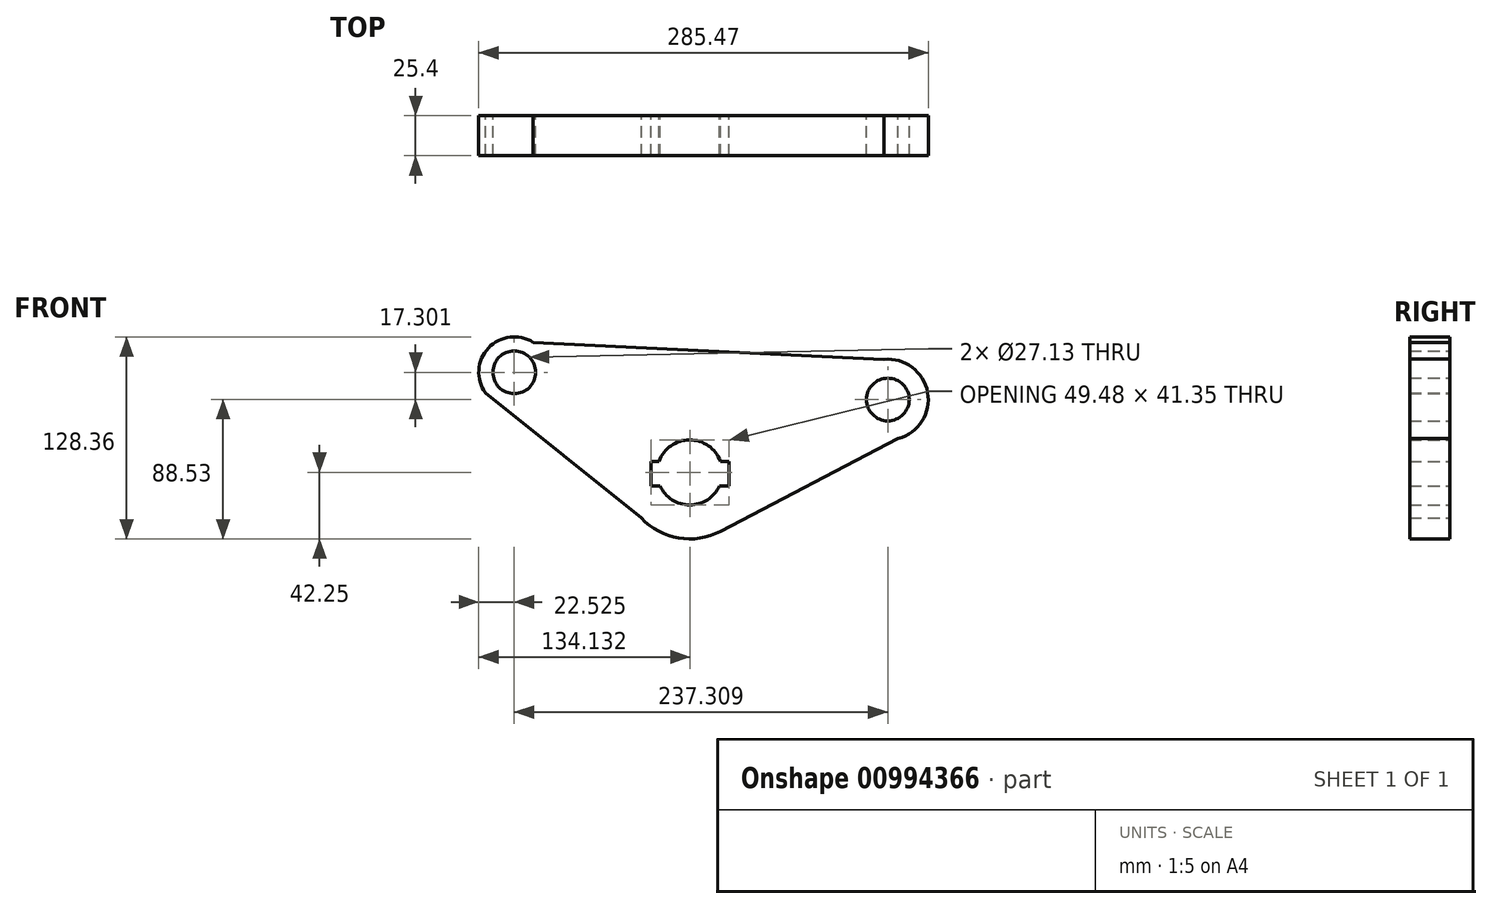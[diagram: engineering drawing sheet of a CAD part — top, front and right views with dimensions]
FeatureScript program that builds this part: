
annotation { "Feature Type Name" : "Feature", "Feature Type Description" : "" }
export const myFeature = defineFeature(function(context is Context, id is Id, definition is map)
    precondition{}
    {
        {
            var Q0;
            Q0=qCreatedBy(makeId("Front.planeOp"),FACE);
            var sketch = newSketch(context, id + "F0", { "sketchPlane" : qUnion([Q0])});
            skCircle(sketch, "E0", {"center": v(0, 0) * mm, "radius": 42.25 * mm});
            skCircle(sketch, "E1", {"center": v(125.87, 46.28) * mm, "radius": 25.63 * mm});
            skLineSegment(sketch, "E2", {"start": v(132.42, 21.5) * mm, "end": v(19.56, -37.45) * mm});
            skCircle(sketch, "E3", {"center": v(0, 0) * mm, "radius": 20.68 * mm});
            skCircle(sketch, "E4", {"center": v(125.87, 46.28) * mm, "radius": 13.56 * mm});
            skCircle(sketch, "E5", {"center": v(-111.44, 63.58) * mm, "radius": 22.52 * mm});
            skLineSegment(sketch, "E6", {"start": v(-99.42, 82.63) * mm, "end": v(123.37, 71.79) * mm});
            skCircle(sketch, "E7", {"center": v(-111.44, 63.58) * mm, "radius": 13.56 * mm});
            skLineSegment(sketch, "E8", {"start": v(-129.8, 50.54) * mm, "end": v(-21.66, -36.28) * mm});
            skLineSegment(sketch, "E9.bottom", {"start": v(-24.57, 7.05) * mm, "end": v(24.91, 7.05) * mm});
            skLineSegment(sketch, "E9.top", {"start": v(-24.57, -8.5) * mm, "end": v(24.91, -8.5) * mm});
            skLineSegment(sketch, "E9.left", {"start": v(-24.57, 7.05) * mm, "end": v(-24.57, -8.5) * mm});
            skLineSegment(sketch, "E9.right", {"start": v(24.91, 7.05) * mm, "end": v(24.91, -8.5) * mm});
            skSolve(sketch);
        }
        {
            var Q0;
            Q0=makeQuery(id+"F0.imprint","IMPRINT",FACE,{"disambiguationData":[TD([[makeQuery(id+"F0.imprint","IMPRINT",EDGE,{"derivedFrom":sQuery(id+"F0.wireOp",EDGE,"E7")}),1.0]])]});
            var Q1;
            Q1=makeQuery(id+"F0.imprint","IMPRINT",FACE,{"disambiguationData":[TD([[makeQuery(id+"F0.imprint","IMPRINT",EDGE,{"derivedFrom":sQuery(id+"F0.wireOp",EDGE,"E7")}),-1.0]])]});
            var Q2;
            {var subQ0=sQuery(id+"F0.wireOp",EDGE,"E9.top");var subQ1=sQuery(id+"F0.wireOp",EDGE,"E3");var subQ2=makeQuery(id+"F0.imprint","INTERSECT",VERTEX,{"disambiguationData":[OD(0.0)],"derivedFrom":[subQ1,subQ0]});Q2=makeQuery(id+"F0.imprint","IMPRINT",FACE,{"disambiguationData":[TD([[makeQuery(id+"F0.imprint","IMPRINT",EDGE,{"disambiguationData":[TD([[subQ2,-1.0]])],"derivedFrom":subQ1}),1.0]])]});}
            var Q3;
            Q3=makeQuery(id+"F0.imprint","IMPRINT",FACE,{"disambiguationData":[TD([[makeQuery(id+"F0.imprint","IMPRINT",EDGE,{"derivedFrom":sQuery(id+"F0.wireOp",EDGE,"E4")}),1.0]])]});
            var Q4;
            {var subQ0=sQuery(id+"F0.wireOp",EDGE,"E9.left");Q4=makeQuery(id+"F0.imprint","IMPRINT",FACE,{"disambiguationData":[TD([[makeQuery(id+"F0.imprint","IMPRINT",EDGE,{"derivedFrom":subQ0}),-1.0]])]});}
            var Q5;
            {var subQ0=sQuery(id+"F0.wireOp",EDGE,"E9.bottom");var subQ1=sQuery(id+"F0.wireOp",EDGE,"E3");var subQ2=makeQuery(id+"F0.imprint","INTERSECT",VERTEX,{"disambiguationData":[OD(0.0)],"derivedFrom":[subQ1,subQ0]});Q5=makeQuery(id+"F0.imprint","IMPRINT",FACE,{"disambiguationData":[TD([[makeQuery(id+"F0.imprint","IMPRINT",EDGE,{"disambiguationData":[TD([[subQ2,-1.0]])],"derivedFrom":subQ1}),1.0]])]});}
            var Q6;
            {var subQ0=sQuery(id+"F0.wireOp",EDGE,"E9.bottom");var subQ1=sQuery(id+"F0.wireOp",EDGE,"E3");var subQ2=makeQuery(id+"F0.imprint","INTERSECT",VERTEX,{"disambiguationData":[OD(0.0)],"derivedFrom":[subQ1,subQ0]});Q6=makeQuery(id+"F0.imprint","IMPRINT",FACE,{"disambiguationData":[TD([[makeQuery(id+"F0.imprint","IMPRINT",EDGE,{"disambiguationData":[TD([[subQ2,1.0]])],"derivedFrom":subQ1}),1.0]])]});}
            var Q7;
            {var subQ0=sQuery(id+"F0.wireOp",EDGE,"E8");var subQ1=sQuery(id+"F0.wireOp",EDGE,"E5");var subQ2=makeQuery(id+"F0.imprint","INTERSECT",VERTEX,{"disambiguationData":[OD(0.0)],"derivedFrom":[subQ1,subQ0]});Q7=makeQuery(id+"F0.imprint","IMPRINT",FACE,{"disambiguationData":[TD([[makeQuery(id+"F0.imprint","IMPRINT",EDGE,{"disambiguationData":[TD([[subQ2,-1.0]])],"derivedFrom":subQ1}),1.0]])]});}
            var Q8;
            {var subQ0=sQuery(id+"F0.wireOp",EDGE,"E8");var subQ1=sQuery(id+"F0.wireOp",EDGE,"E0");var subQ2=makeQuery(id+"F0.imprint","INTERSECT",VERTEX,{"disambiguationData":[OD(0.0)],"derivedFrom":[subQ1,subQ0]});Q8=makeQuery(id+"F0.imprint","IMPRINT",FACE,{"disambiguationData":[TD([[makeQuery(id+"F0.imprint","IMPRINT",EDGE,{"disambiguationData":[TD([[subQ2,1.0]])],"derivedFrom":subQ1}),1.0]])]});}
            var Q9;
            {var subQ5=sQuery(id+"F0.wireOp",EDGE,"E9.right");Q9=makeQuery(id+"F0.imprint","IMPRINT",FACE,{"disambiguationData":[TD([[makeQuery(id+"F0.imprint","IMPRINT",EDGE,{"derivedFrom":subQ5}),-1.0]])]});}
            var Q10;
            {var subQ5=sQuery(id+"F0.wireOp",EDGE,"E9.left");Q10=makeQuery(id+"F0.imprint","IMPRINT",FACE,{"disambiguationData":[TD([[makeQuery(id+"F0.imprint","IMPRINT",EDGE,{"derivedFrom":subQ5}),1.0]])]});}
            var Q11;
            Q11=makeQuery(id+"F0.imprint","IMPRINT",FACE,{"disambiguationData":[TD([[makeQuery(id+"F0.imprint","IMPRINT",EDGE,{"derivedFrom":sQuery(id+"F0.wireOp",EDGE,"E4")}),-1.0]])]});
            var Q12;
            {var subQ0=sQuery(id+"F0.wireOp",EDGE,"E2");Q12=makeQuery(id+"F0.imprint","IMPRINT",FACE,{"disambiguationData":[TD([[makeQuery(id+"F0.imprint","IMPRINT",EDGE,{"derivedFrom":subQ0}),-1.0]])]});}
            extrude(context, id + "F1", {"entities" : qUnion([Q0, Q1, Q2, Q3, Q4, Q5, Q6, Q7, Q8, Q9, Q10, Q11, Q12]), "depth" : 25.4 * mm, "offsetDistance" : 25.4 * mm});
        }
        {
            var Q0;
            {var subQ0=sQuery(id+"F0.wireOp",EDGE,"E9.top");var subQ1=sQuery(id+"F0.wireOp",EDGE,"E3");var subQ2=makeQuery(id+"F0.imprint","INTERSECT",VERTEX,{"disambiguationData":[OD(0.0)],"derivedFrom":[subQ1,subQ0]});Q0=makeQuery(id+"F0.imprint","IMPRINT",FACE,{"disambiguationData":[TD([[makeQuery(id+"F0.imprint","IMPRINT",EDGE,{"disambiguationData":[TD([[subQ2,-1.0]])],"derivedFrom":subQ1}),1.0]])]});}
            var Q1;
            {var subQ0=sQuery(id+"F0.wireOp",EDGE,"E9.bottom");var subQ1=sQuery(id+"F0.wireOp",EDGE,"E3");var subQ2=makeQuery(id+"F0.imprint","INTERSECT",VERTEX,{"disambiguationData":[OD(0.0)],"derivedFrom":[subQ1,subQ0]});Q1=makeQuery(id+"F0.imprint","IMPRINT",FACE,{"disambiguationData":[TD([[makeQuery(id+"F0.imprint","IMPRINT",EDGE,{"disambiguationData":[TD([[subQ2,-1.0]])],"derivedFrom":subQ1}),1.0]])]});}
            var Q2;
            {var subQ5=sQuery(id+"F0.wireOp",EDGE,"E9.left");Q2=makeQuery(id+"F0.imprint","IMPRINT",FACE,{"disambiguationData":[TD([[makeQuery(id+"F0.imprint","IMPRINT",EDGE,{"derivedFrom":subQ5}),1.0]])]});}
            var Q3;
            {var subQ5=sQuery(id+"F0.wireOp",EDGE,"E9.right");Q3=makeQuery(id+"F0.imprint","IMPRINT",FACE,{"disambiguationData":[TD([[makeQuery(id+"F0.imprint","IMPRINT",EDGE,{"derivedFrom":subQ5}),-1.0]])]});}
            var Q4;
            {var subQ0=sQuery(id+"F0.wireOp",EDGE,"E9.bottom");var subQ1=sQuery(id+"F0.wireOp",EDGE,"E3");var subQ2=makeQuery(id+"F0.imprint","INTERSECT",VERTEX,{"disambiguationData":[OD(0.0)],"derivedFrom":[subQ1,subQ0]});Q4=makeQuery(id+"F0.imprint","IMPRINT",FACE,{"disambiguationData":[TD([[makeQuery(id+"F0.imprint","IMPRINT",EDGE,{"disambiguationData":[TD([[subQ2,1.0]])],"derivedFrom":subQ1}),1.0]])]});}
            extrude(context, id + "F2", {"entities" : qUnion([Q0, Q1, Q2, Q3, Q4]), "operationType" : NewBodyOperationType.REMOVE, "depth" : 41.66 * mm, "offsetDistance" : 25.4 * mm});
        }
        {
            var Q0;
            Q0=makeQuery(id+"F0.imprint","IMPRINT",FACE,{"disambiguationData":[TD([[makeQuery(id+"F0.imprint","IMPRINT",EDGE,{"derivedFrom":sQuery(id+"F0.wireOp",EDGE,"E7")}),1.0]])]});
            var Q1;
            Q1=makeQuery(id+"F0.imprint","IMPRINT",FACE,{"disambiguationData":[TD([[makeQuery(id+"F0.imprint","IMPRINT",EDGE,{"derivedFrom":sQuery(id+"F0.wireOp",EDGE,"E4")}),1.0]])]});
            extrude(context, id + "F3", {"entities" : qUnion([Q0, Q1]), "operationType" : NewBodyOperationType.REMOVE, "depth" : 26.16 * mm, "offsetDistance" : 25.4 * mm});
        }
    });
